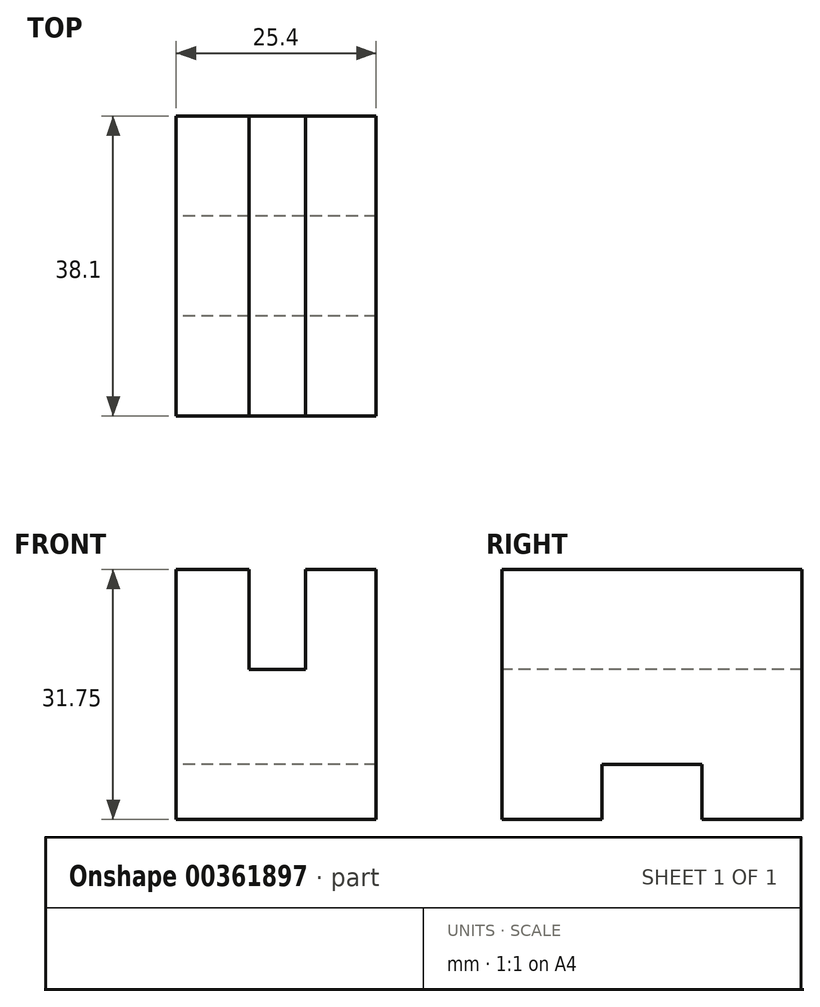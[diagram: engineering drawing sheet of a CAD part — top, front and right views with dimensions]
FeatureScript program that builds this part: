
annotation { "Feature Type Name" : "Feature", "Feature Type Description" : "" }
export const myFeature = defineFeature(function(context is Context, id is Id, definition is map)
    precondition{}
    {
        {
            var Q0;
            Q0=qCreatedBy(makeId("Right.planeOp"),FACE);
            var sketch = newSketch(context, id + "F0", { "sketchPlane" : qUnion([Q0])});
            skLineSegment(sketch, "E0", {"start": v(0, 0) * mm, "end": v(12.7, 0) * mm});
            skLineSegment(sketch, "E1", {"start": v(12.7, 0) * mm, "end": v(12.7, 31.75) * mm});
            skLineSegment(sketch, "E2", {"start": v(12.7, 31.75) * mm, "end": v(-25.4, 31.75) * mm});
            skLineSegment(sketch, "E3", {"start": v(-25.4, 31.75) * mm, "end": v(-25.4, 0) * mm});
            skLineSegment(sketch, "E4", {"start": v(-25.4, 0) * mm, "end": v(-12.7, 0) * mm});
            skLineSegment(sketch, "E5", {"start": v(-12.7, 0) * mm, "end": v(-12.7, 6.98) * mm});
            skLineSegment(sketch, "E6", {"start": v(-12.7, 6.98) * mm, "end": v(0, 6.98) * mm});
            skLineSegment(sketch, "E7", {"start": v(0, 6.98) * mm, "end": v(0, 0) * mm});
            skSolve(sketch);
        }
        {
            var Q0;
            Q0 = qSketchRegion(id + "F0", true);
            extrude(context, id + "F1", {"entities" : qUnion([Q0]), "depth" : 25.4 * mm});
        }
        {
            var Q0;
            Q0=makeQuery(id+"F1.opExtrude","SWEPT_FACE",FACE,{"disambiguationData":[OSD([sQuery(id+"F0.wireOp",EDGE,"E2")])]});
            var sketch = newSketch(context, id + "F2", { "sketchPlane" : qUnion([Q0])});
            skLineSegment(sketch, "E8", {"start": v(9.29, 12.7) * mm, "end": v(9.29, -25.4) * mm});
            skLineSegment(sketch, "E9", {"start": v(16.4, 12.7) * mm, "end": v(16.4, -25.4) * mm});
            skSolve(sketch);
        }
        {
            var Q0;
            Q0 = qSketchRegion(id + "F2", true);
            var Q1;
            {var subQ0=sQuery(id+"F2.wireOp",EDGE,"E8");Q1=makeQuery(id+"F2.imprint","IMPRINT",FACE,{"disambiguationData":[TD([[makeQuery(id+"F2.imprint","IMPRINT",EDGE,{"derivedFrom":subQ0}),1.0]])]});}
            extrude(context, id + "F3", {"entities" : qUnion([Q0, Q1]), "operationType" : NewBodyOperationType.REMOVE, "oppositeDirection" : true, "depth" : 12.7 * mm});
        }
    });
